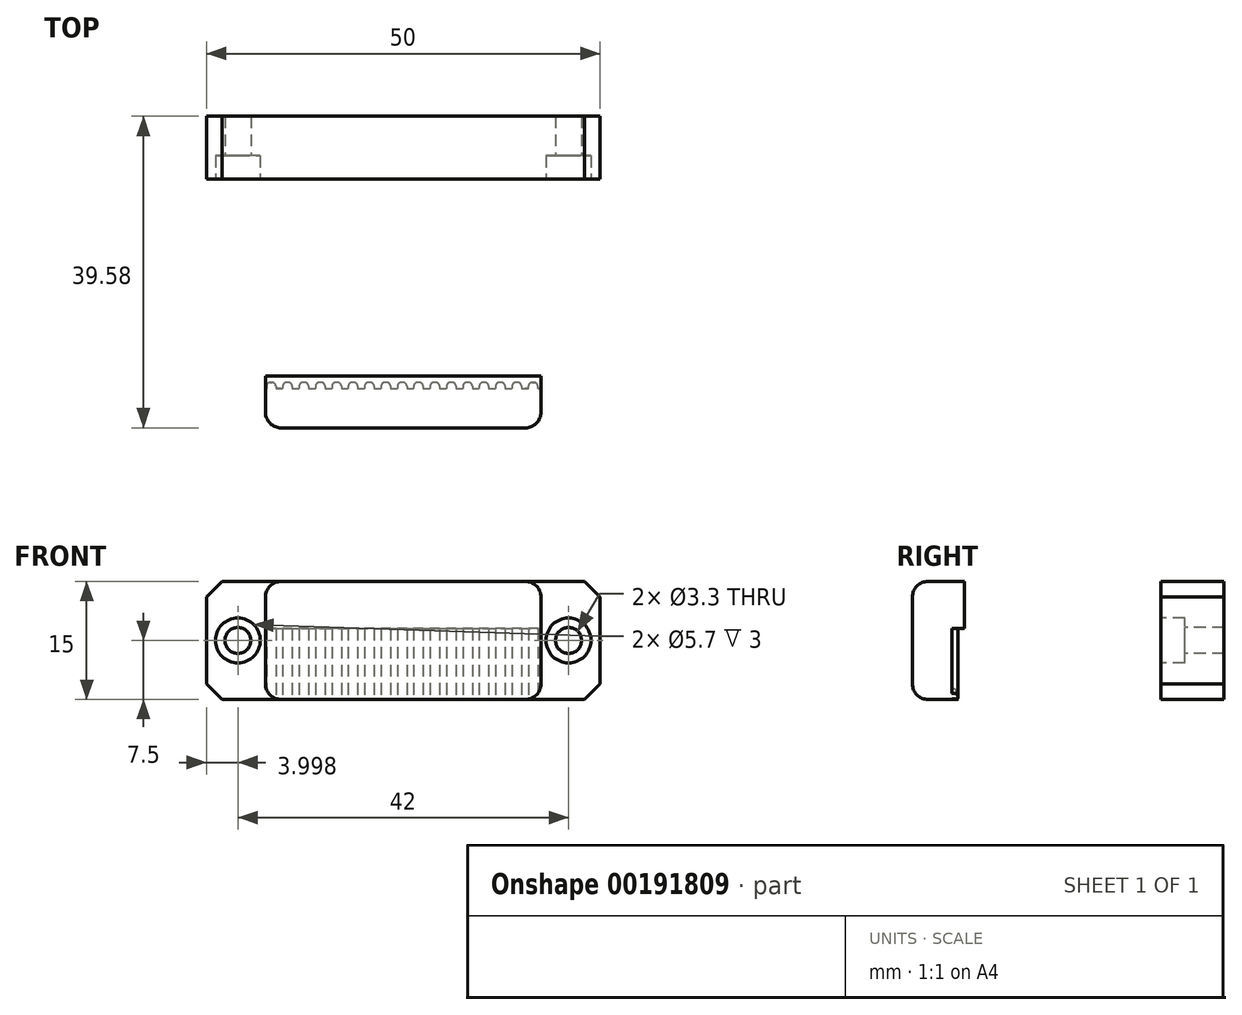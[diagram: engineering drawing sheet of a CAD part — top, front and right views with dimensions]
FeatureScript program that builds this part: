
annotation { "Feature Type Name" : "Feature", "Feature Type Description" : "" }
export const myFeature = defineFeature(function(context is Context, id is Id, definition is map)
    precondition{}
    {
        {
            var Q0;
            Q0=qCreatedBy(makeId("Top.planeOp"),FACE);
            var sketch = newSketch(context, id + "F0", { "sketchPlane" : qUnion([Q0])});
            skLineSegment(sketch, "E0.bottom", {"start": v(-21.77, 12.22) * mm, "end": v(28.23, 12.22) * mm});
            skLineSegment(sketch, "E0.top", {"start": v(-21.77, 4.22) * mm, "end": v(28.23, 4.22) * mm});
            skLineSegment(sketch, "E0.left", {"start": v(-21.77, 12.22) * mm, "end": v(-21.77, 4.22) * mm});
            skLineSegment(sketch, "E0.right", {"start": v(28.23, 12.22) * mm, "end": v(28.23, 4.22) * mm});
            skLineSegment(sketch, "E1.bottom", {"start": v(-14.27, 4.22) * mm, "end": v(20.73, 4.22) * mm});
            skLineSegment(sketch, "E1.top", {"start": v(-14.27, -20.78) * mm, "end": v(20.73, -20.78) * mm});
            skLineSegment(sketch, "E1.left", {"start": v(-14.27, 4.22) * mm, "end": v(-14.27, -20.78) * mm});
            skLineSegment(sketch, "E1.right", {"start": v(20.73, 4.22) * mm, "end": v(20.73, -20.78) * mm});
            skLineSegment(sketch, "E2.top", {"start": v(-14.27, -22.36) * mm, "end": v(20.73, -22.36) * mm});
            skLineSegment(sketch, "E2.left", {"start": v(-14.27, -20.78) * mm, "end": v(-14.27, -22.36) * mm});
            skLineSegment(sketch, "E2.right", {"start": v(20.73, -20.78) * mm, "end": v(20.73, -22.36) * mm});
            skLineSegment(sketch, "E3.top", {"start": v(-14.27, -27.36) * mm, "end": v(20.73, -27.36) * mm});
            skLineSegment(sketch, "E3.left", {"start": v(-14.27, -22.36) * mm, "end": v(-14.27, -27.36) * mm});
            skLineSegment(sketch, "E3.right", {"start": v(20.73, -22.36) * mm, "end": v(20.73, -27.36) * mm});
            skSolve(sketch);
        }
        {
            var Q0;
            Q0=makeQuery(id+"F0.imprint","IMPRINT",FACE,{"disambiguationData":[TD([[makeQuery(id+"F0.imprint","IMPRINT",EDGE,{"derivedFrom":sQuery(id+"F0.wireOp",EDGE,"E0.bottom")}),-1.0]])]});
            var Q1;
            Q1=makeQuery(id+"F0.imprint","IMPRINT",FACE,{"disambiguationData":[TD([[makeQuery(id+"F0.imprint","IMPRINT",EDGE,{"derivedFrom":sQuery(id+"F0.wireOp",EDGE,"E1.bottom")}),-1.0]])]});
            var Q2;
            Q2=makeQuery(id+"F0.imprint","IMPRINT",FACE,{"disambiguationData":[TD([[makeQuery(id+"F0.imprint","IMPRINT",EDGE,{"derivedFrom":sQuery(id+"F0.wireOp",EDGE,"E1.top")}),-1.0]])]});
            var Q3;
            Q3=makeQuery(id+"F0.imprint","IMPRINT",FACE,{"disambiguationData":[TD([[makeQuery(id+"F0.imprint","IMPRINT",EDGE,{"derivedFrom":sQuery(id+"F0.wireOp",EDGE,"E2.top")}),-1.0]])]});
            extrude(context, id + "F1", {"entities" : qUnion([Q0, Q1, Q2, Q3]), "depth" : 15 * mm});
        }
        {
            var Q0;
            Q0=makeQuery(id+"F0.imprint","IMPRINT",FACE,{"disambiguationData":[TD([[makeQuery(id+"F0.imprint","IMPRINT",EDGE,{"derivedFrom":sQuery(id+"F0.wireOp",EDGE,"E1.top")}),-1.0]])]});
            var sketch = newSketch(context, id + "F2", { "sketchPlane" : qUnion([Q0])});
            skLineSegment(sketch, "E4", {"start": v(19.88, -21.6) * mm, "end": v(-14.27, -21.6) * mm, "construction": true});
            skLineSegment(sketch, "E5.bottom", {"start": v(20.32, -21.6) * mm, "end": v(19.58, -21.6) * mm});
            skLineSegment(sketch, "E5.top", {"start": v(20.33, -22.36) * mm, "end": v(19.13, -22.36) * mm});
            skLineSegment(sketch, "E5.left", {"start": v(20.33, -22.06) * mm, "end": v(20.33, -22.36) * mm});
            skLineSegment(sketch, "E5.right", {"start": v(19.13, -22.06) * mm, "end": v(19.13, -22.36) * mm});
            skLineSegment(sketch, "E6.bottom", {"start": v(17.8, -21.6) * mm, "end": v(17.5, -21.6) * mm});
            skLineSegment(sketch, "E6.top", {"start": v(18.25, -22.36) * mm, "end": v(17.05, -22.36) * mm});
            skLineSegment(sketch, "E6.left", {"start": v(18.25, -22.06) * mm, "end": v(18.25, -22.36) * mm});
            skLineSegment(sketch, "E6.right", {"start": v(17.05, -22.06) * mm, "end": v(17.05, -22.36) * mm});
            skLineSegment(sketch, "E7.bottom", {"start": v(15.72, -21.6) * mm, "end": v(15.42, -21.6) * mm});
            skLineSegment(sketch, "E7.top", {"start": v(16.17, -22.36) * mm, "end": v(14.97, -22.36) * mm});
            skLineSegment(sketch, "E7.left", {"start": v(16.17, -22.06) * mm, "end": v(16.17, -22.36) * mm});
            skLineSegment(sketch, "E7.right", {"start": v(14.97, -22.06) * mm, "end": v(14.97, -22.36) * mm});
            skLineSegment(sketch, "E8.bottom", {"start": v(13.64, -21.6) * mm, "end": v(13.34, -21.6) * mm});
            skLineSegment(sketch, "E8.top", {"start": v(14.09, -22.36) * mm, "end": v(12.89, -22.36) * mm});
            skLineSegment(sketch, "E8.left", {"start": v(14.09, -22.06) * mm, "end": v(14.09, -22.36) * mm});
            skLineSegment(sketch, "E8.right", {"start": v(12.89, -22.06) * mm, "end": v(12.89, -22.36) * mm});
            skLineSegment(sketch, "E9.bottom", {"start": v(11.56, -21.6) * mm, "end": v(11.26, -21.6) * mm});
            skLineSegment(sketch, "E9.top", {"start": v(12, -22.36) * mm, "end": v(10.8, -22.36) * mm});
            skLineSegment(sketch, "E9.left", {"start": v(12, -22.06) * mm, "end": v(12, -22.36) * mm});
            skLineSegment(sketch, "E9.right", {"start": v(10.8, -22.06) * mm, "end": v(10.8, -22.36) * mm});
            skLineSegment(sketch, "E10.bottom", {"start": v(9.48, -21.6) * mm, "end": v(9.18, -21.6) * mm});
            skLineSegment(sketch, "E10.top", {"start": v(9.93, -22.36) * mm, "end": v(8.73, -22.36) * mm});
            skLineSegment(sketch, "E10.left", {"start": v(9.93, -22.06) * mm, "end": v(9.93, -22.36) * mm});
            skLineSegment(sketch, "E10.right", {"start": v(8.73, -22.06) * mm, "end": v(8.73, -22.36) * mm});
            skLineSegment(sketch, "E11.bottom", {"start": v(7.4, -21.6) * mm, "end": v(7.1, -21.6) * mm});
            skLineSegment(sketch, "E11.top", {"start": v(7.85, -22.36) * mm, "end": v(6.65, -22.36) * mm});
            skLineSegment(sketch, "E11.left", {"start": v(7.85, -22.06) * mm, "end": v(7.85, -22.36) * mm});
            skLineSegment(sketch, "E11.right", {"start": v(6.65, -22.06) * mm, "end": v(6.65, -22.36) * mm});
            skLineSegment(sketch, "E12.bottom", {"start": v(5.32, -21.6) * mm, "end": v(5.02, -21.6) * mm});
            skLineSegment(sketch, "E12.top", {"start": v(5.77, -22.36) * mm, "end": v(4.57, -22.36) * mm});
            skLineSegment(sketch, "E12.left", {"start": v(5.77, -22.06) * mm, "end": v(5.77, -22.36) * mm});
            skLineSegment(sketch, "E12.right", {"start": v(4.57, -22.06) * mm, "end": v(4.57, -22.36) * mm});
            skLineSegment(sketch, "E13.bottom", {"start": v(3.24, -21.6) * mm, "end": v(2.94, -21.6) * mm});
            skLineSegment(sketch, "E13.top", {"start": v(3.69, -22.36) * mm, "end": v(2.49, -22.36) * mm});
            skLineSegment(sketch, "E13.left", {"start": v(3.69, -22.06) * mm, "end": v(3.69, -22.36) * mm});
            skLineSegment(sketch, "E13.right", {"start": v(2.49, -22.06) * mm, "end": v(2.49, -22.36) * mm});
            skLineSegment(sketch, "E14.bottom", {"start": v(1.16, -21.6) * mm, "end": v(0.86, -21.6) * mm});
            skLineSegment(sketch, "E14.top", {"start": v(1.6, -22.36) * mm, "end": v(0.4, -22.36) * mm});
            skLineSegment(sketch, "E14.left", {"start": v(1.6, -22.06) * mm, "end": v(1.6, -22.36) * mm});
            skLineSegment(sketch, "E14.right", {"start": v(0.4, -22.06) * mm, "end": v(0.4, -22.36) * mm});
            skLineSegment(sketch, "E15.bottom", {"start": v(-0.92, -21.6) * mm, "end": v(-1.22, -21.6) * mm});
            skLineSegment(sketch, "E15.top", {"start": v(-0.47, -22.36) * mm, "end": v(-1.67, -22.36) * mm});
            skLineSegment(sketch, "E15.left", {"start": v(-0.47, -22.06) * mm, "end": v(-0.47, -22.36) * mm});
            skLineSegment(sketch, "E15.right", {"start": v(-1.67, -22.06) * mm, "end": v(-1.67, -22.36) * mm});
            skLineSegment(sketch, "E16.bottom", {"start": v(-3, -21.6) * mm, "end": v(-3.3, -21.6) * mm});
            skLineSegment(sketch, "E16.top", {"start": v(-2.55, -22.36) * mm, "end": v(-3.75, -22.36) * mm});
            skLineSegment(sketch, "E16.left", {"start": v(-2.55, -22.06) * mm, "end": v(-2.55, -22.36) * mm});
            skLineSegment(sketch, "E16.right", {"start": v(-3.75, -22.06) * mm, "end": v(-3.75, -22.36) * mm});
            skLineSegment(sketch, "E17.bottom", {"start": v(-5.08, -21.6) * mm, "end": v(-5.38, -21.6) * mm});
            skLineSegment(sketch, "E17.top", {"start": v(-4.63, -22.36) * mm, "end": v(-5.83, -22.36) * mm});
            skLineSegment(sketch, "E17.left", {"start": v(-4.63, -22.06) * mm, "end": v(-4.63, -22.36) * mm});
            skLineSegment(sketch, "E17.right", {"start": v(-5.83, -22.06) * mm, "end": v(-5.83, -22.36) * mm});
            skLineSegment(sketch, "E18.bottom", {"start": v(-7.16, -21.6) * mm, "end": v(-7.46, -21.6) * mm});
            skLineSegment(sketch, "E18.top", {"start": v(-6.71, -22.36) * mm, "end": v(-7.91, -22.36) * mm});
            skLineSegment(sketch, "E18.left", {"start": v(-6.71, -22.06) * mm, "end": v(-6.71, -22.36) * mm});
            skLineSegment(sketch, "E18.right", {"start": v(-7.91, -22.06) * mm, "end": v(-7.91, -22.36) * mm});
            skLineSegment(sketch, "E19.bottom", {"start": v(-9.24, -21.6) * mm, "end": v(-9.54, -21.6) * mm});
            skLineSegment(sketch, "E19.top", {"start": v(-8.8, -22.36) * mm, "end": v(-10, -22.36) * mm});
            skLineSegment(sketch, "E19.left", {"start": v(-8.8, -22.06) * mm, "end": v(-8.8, -22.36) * mm});
            skLineSegment(sketch, "E19.right", {"start": v(-10, -22.06) * mm, "end": v(-10, -22.36) * mm});
            skLineSegment(sketch, "E20.bottom", {"start": v(-11.32, -21.6) * mm, "end": v(-11.62, -21.6) * mm});
            skLineSegment(sketch, "E20.top", {"start": v(-10.87, -22.36) * mm, "end": v(-12.07, -22.36) * mm});
            skLineSegment(sketch, "E20.left", {"start": v(-10.87, -22.06) * mm, "end": v(-10.87, -22.36) * mm});
            skLineSegment(sketch, "E20.right", {"start": v(-12.07, -22.06) * mm, "end": v(-12.07, -22.36) * mm});
            skLineSegment(sketch, "E21.bottom", {"start": v(-13.4, -21.6) * mm, "end": v(-13.7, -21.6) * mm});
            skLineSegment(sketch, "E21.top", {"start": v(-12.95, -22.36) * mm, "end": v(-14.15, -22.36) * mm});
            skLineSegment(sketch, "E21.left", {"start": v(-12.95, -22.06) * mm, "end": v(-12.95, -22.36) * mm});
            skLineSegment(sketch, "E21.right", {"start": v(-14.15, -22.06) * mm, "end": v(-14.15, -22.36) * mm});
            skLineSegment(sketch, "E22.bottom", {"start": v(-12.41, -21.6) * mm, "end": v(-13.61, -21.6) * mm});
            skPoint(sketch, "E23.newPointB", {"position": v(20.73, -21.6) * mm});
            skArc(sketch, "E23.filletArc", {"start": v(20.33, -22.06) * mm, "mid": v(20.2, -21.74) * mm, "end": v(19.88, -21.6) * mm});
            skPoint(sketch, "E24.visualSharp", {"position": v(19.13, -21.6) * mm});
            skArc(sketch, "E24.filletArc", {"start": v(19.58, -21.6) * mm, "mid": v(19.26, -21.74) * mm, "end": v(19.13, -22.06) * mm});
            skPoint(sketch, "E25.visualSharp", {"position": v(18.25, -21.6) * mm});
            skArc(sketch, "E25.filletArc", {"start": v(18.25, -22.06) * mm, "mid": v(18.12, -21.74) * mm, "end": v(17.8, -21.6) * mm});
            skPoint(sketch, "E26.visualSharp", {"position": v(17.05, -21.6) * mm});
            skArc(sketch, "E26.filletArc", {"start": v(17.5, -21.6) * mm, "mid": v(17.18, -21.74) * mm, "end": v(17.05, -22.06) * mm});
            skPoint(sketch, "E27.visualSharp", {"position": v(16.17, -21.6) * mm});
            skArc(sketch, "E27.filletArc", {"start": v(16.17, -22.06) * mm, "mid": v(16.04, -21.74) * mm, "end": v(15.72, -21.6) * mm});
            skPoint(sketch, "E28.visualSharp", {"position": v(14.97, -21.6) * mm});
            skArc(sketch, "E28.filletArc", {"start": v(15.42, -21.6) * mm, "mid": v(15.1, -21.74) * mm, "end": v(14.97, -22.06) * mm});
            skPoint(sketch, "E29.visualSharp", {"position": v(14.09, -21.6) * mm});
            skArc(sketch, "E29.filletArc", {"start": v(14.09, -22.06) * mm, "mid": v(13.96, -21.74) * mm, "end": v(13.64, -21.6) * mm});
            skPoint(sketch, "E30.visualSharp", {"position": v(12.89, -21.6) * mm});
            skArc(sketch, "E30.filletArc", {"start": v(13.34, -21.6) * mm, "mid": v(13.02, -21.74) * mm, "end": v(12.89, -22.06) * mm});
            skPoint(sketch, "E31.visualSharp", {"position": v(12, -21.6) * mm});
            skArc(sketch, "E31.filletArc", {"start": v(12, -22.06) * mm, "mid": v(11.88, -21.74) * mm, "end": v(11.56, -21.6) * mm});
            skPoint(sketch, "E32.visualSharp", {"position": v(10.8, -21.6) * mm});
            skArc(sketch, "E32.filletArc", {"start": v(11.26, -21.6) * mm, "mid": v(10.94, -21.74) * mm, "end": v(10.8, -22.06) * mm});
            skPoint(sketch, "E33.visualSharp", {"position": v(9.93, -21.6) * mm});
            skArc(sketch, "E33.filletArc", {"start": v(9.93, -22.06) * mm, "mid": v(9.8, -21.74) * mm, "end": v(9.48, -21.6) * mm});
            skPoint(sketch, "E34.visualSharp", {"position": v(8.73, -21.6) * mm});
            skArc(sketch, "E34.filletArc", {"start": v(9.18, -21.6) * mm, "mid": v(8.86, -21.74) * mm, "end": v(8.73, -22.06) * mm});
            skPoint(sketch, "E35.visualSharp", {"position": v(7.85, -21.6) * mm});
            skArc(sketch, "E35.filletArc", {"start": v(7.85, -22.06) * mm, "mid": v(7.72, -21.74) * mm, "end": v(7.4, -21.6) * mm});
            skPoint(sketch, "E36.visualSharp", {"position": v(6.65, -21.6) * mm});
            skArc(sketch, "E36.filletArc", {"start": v(7.1, -21.6) * mm, "mid": v(6.78, -21.74) * mm, "end": v(6.65, -22.06) * mm});
            skPoint(sketch, "E37.visualSharp", {"position": v(5.77, -21.6) * mm});
            skArc(sketch, "E37.filletArc", {"start": v(5.77, -22.06) * mm, "mid": v(5.64, -21.74) * mm, "end": v(5.32, -21.6) * mm});
            skPoint(sketch, "E38.visualSharp", {"position": v(4.57, -21.6) * mm});
            skArc(sketch, "E38.filletArc", {"start": v(5.02, -21.6) * mm, "mid": v(4.7, -21.74) * mm, "end": v(4.57, -22.06) * mm});
            skPoint(sketch, "E39.visualSharp", {"position": v(3.69, -21.6) * mm});
            skArc(sketch, "E39.filletArc", {"start": v(3.69, -22.06) * mm, "mid": v(3.56, -21.74) * mm, "end": v(3.24, -21.6) * mm});
            skPoint(sketch, "E40.visualSharp", {"position": v(1.6, -21.6) * mm});
            skArc(sketch, "E40.filletArc", {"start": v(1.6, -22.06) * mm, "mid": v(1.48, -21.74) * mm, "end": v(1.16, -21.6) * mm});
            skPoint(sketch, "E41.visualSharp", {"position": v(2.49, -21.6) * mm});
            skArc(sketch, "E41.filletArc", {"start": v(2.94, -21.6) * mm, "mid": v(2.62, -21.74) * mm, "end": v(2.49, -22.06) * mm});
            skPoint(sketch, "E42.visualSharp", {"position": v(0.4, -21.6) * mm});
            skArc(sketch, "E42.filletArc", {"start": v(0.86, -21.6) * mm, "mid": v(0.54, -21.74) * mm, "end": v(0.4, -22.06) * mm});
            skPoint(sketch, "E43.visualSharp", {"position": v(-0.47, -21.6) * mm});
            skArc(sketch, "E43.filletArc", {"start": v(-0.47, -22.06) * mm, "mid": v(-0.6, -21.74) * mm, "end": v(-0.92, -21.6) * mm});
            skPoint(sketch, "E44.visualSharp", {"position": v(-1.67, -21.6) * mm});
            skArc(sketch, "E44.filletArc", {"start": v(-1.22, -21.6) * mm, "mid": v(-1.54, -21.74) * mm, "end": v(-1.67, -22.06) * mm});
            skPoint(sketch, "E45.visualSharp", {"position": v(-2.55, -21.6) * mm});
            skArc(sketch, "E45.filletArc", {"start": v(-2.55, -22.06) * mm, "mid": v(-2.68, -21.74) * mm, "end": v(-3, -21.6) * mm});
            skPoint(sketch, "E46.visualSharp", {"position": v(-3.75, -21.6) * mm});
            skArc(sketch, "E46.filletArc", {"start": v(-3.3, -21.6) * mm, "mid": v(-3.62, -21.74) * mm, "end": v(-3.75, -22.06) * mm});
            skPoint(sketch, "E47.visualSharp", {"position": v(-4.63, -21.6) * mm});
            skArc(sketch, "E47.filletArc", {"start": v(-4.63, -22.06) * mm, "mid": v(-4.76, -21.74) * mm, "end": v(-5.08, -21.6) * mm});
            skPoint(sketch, "E48.visualSharp", {"position": v(-5.83, -21.6) * mm});
            skArc(sketch, "E48.filletArc", {"start": v(-5.38, -21.6) * mm, "mid": v(-5.7, -21.74) * mm, "end": v(-5.83, -22.06) * mm});
            skPoint(sketch, "E49.visualSharp", {"position": v(-6.71, -21.6) * mm});
            skArc(sketch, "E49.filletArc", {"start": v(-6.71, -22.06) * mm, "mid": v(-6.84, -21.74) * mm, "end": v(-7.16, -21.6) * mm});
            skPoint(sketch, "E50.visualSharp", {"position": v(-7.91, -21.6) * mm});
            skArc(sketch, "E50.filletArc", {"start": v(-7.46, -21.6) * mm, "mid": v(-7.78, -21.74) * mm, "end": v(-7.91, -22.06) * mm});
            skPoint(sketch, "E51.visualSharp", {"position": v(-8.8, -21.6) * mm});
            skArc(sketch, "E51.filletArc", {"start": v(-8.8, -22.06) * mm, "mid": v(-8.92, -21.74) * mm, "end": v(-9.24, -21.6) * mm});
            skPoint(sketch, "E52.visualSharp", {"position": v(-10, -21.6) * mm});
            skArc(sketch, "E52.filletArc", {"start": v(-9.54, -21.6) * mm, "mid": v(-9.86, -21.74) * mm, "end": v(-10, -22.06) * mm});
            skPoint(sketch, "E53.visualSharp", {"position": v(-10.87, -21.6) * mm});
            skArc(sketch, "E53.filletArc", {"start": v(-10.87, -22.06) * mm, "mid": v(-11, -21.74) * mm, "end": v(-11.32, -21.6) * mm});
            skPoint(sketch, "E54.visualSharp", {"position": v(-12.07, -21.6) * mm});
            skArc(sketch, "E54.filletArc", {"start": v(-11.62, -21.6) * mm, "mid": v(-11.94, -21.74) * mm, "end": v(-12.07, -22.06) * mm});
            skPoint(sketch, "E55.visualSharp", {"position": v(-12.95, -21.6) * mm});
            skArc(sketch, "E55.filletArc", {"start": v(-12.95, -22.06) * mm, "mid": v(-13.08, -21.74) * mm, "end": v(-13.4, -21.6) * mm});
            skPoint(sketch, "E56.visualSharp", {"position": v(-14.15, -21.6) * mm});
            skArc(sketch, "E56.filletArc", {"start": v(-13.7, -21.6) * mm, "mid": v(-14.02, -21.74) * mm, "end": v(-14.15, -22.06) * mm});
            skSolve(sketch);
        }
        {
            var Q0;
            {var subQ10=sQuery(id+"F2.wireOp",EDGE,"E5.left");Q0=makeQuery(id+"F2.imprint","IMPRINT",FACE,{"disambiguationData":[TD([[makeQuery(id+"F2.imprint","IMPRINT",EDGE,{"derivedFrom":subQ10}),1.0]])]});}
            extrude(context, id + "F3", {"entities" : qUnion([Q0]), "operationType" : NewBodyOperationType.REMOVE, "depth" : 9 * mm});
        }
        {
            var Q0;
            {var subQ0=sQuery(id+"F0.wireOp",EDGE,"E3.left");var subQ1=sQuery(id+"F0.wireOp",EDGE,"E2.left");var subQ2=sQuery(id+"F0.wireOp",EDGE,"E1.left");Q0=makeQuery(id+"F3.boolean.opBoolean","SPLIT",EDGE,{"disambiguationData":[TD([makeQuery(id+"F3.opExtrude","SWEPT_FACE",FACE,{"disambiguationData":[OSD([sQuery(id+"F0.wireOp",EDGE,"E1.top")])]})])],"derivedFrom":makeQuery(id+"F1.opExtrude","CAP_EDGE",EDGE,{"disambiguationData":[OSD([subQ2,subQ1,subQ0])],"isStart":true})});}
            var Q1;
            Q1=makeQuery(id+"F1.opExtrude","CAP_EDGE",EDGE,{"disambiguationData":[OSD([sQuery(id+"F0.wireOp",EDGE,"E1.left"),sQuery(id+"F0.wireOp",EDGE,"E2.left"),sQuery(id+"F0.wireOp",EDGE,"E3.left")])],"isStart":false});
            var Q2;
            Q2=makeQuery(id+"F1.opExtrude","CAP_EDGE",EDGE,{"disambiguationData":[OSD([sQuery(id+"F0.wireOp",EDGE,"E1.right"),sQuery(id+"F0.wireOp",EDGE,"E2.right"),sQuery(id+"F0.wireOp",EDGE,"E3.right")])],"isStart":false});
            var Q3;
            {var subQ0=sQuery(id+"F0.wireOp",EDGE,"E3.right");var subQ1=sQuery(id+"F0.wireOp",EDGE,"E2.right");var subQ2=sQuery(id+"F0.wireOp",EDGE,"E1.right");Q3=makeQuery(id+"F3.boolean.opBoolean","SPLIT",EDGE,{"disambiguationData":[TD([makeQuery(id+"F3.opExtrude","SWEPT_FACE",FACE,{"disambiguationData":[OSD([sQuery(id+"F0.wireOp",EDGE,"E1.top")])]})])],"derivedFrom":makeQuery(id+"F1.opExtrude","CAP_EDGE",EDGE,{"disambiguationData":[OSD([subQ2,subQ1,subQ0])],"isStart":true})});}
            var Q4;
            Q4=makeQuery(id+"F1.opExtrude","CAP_EDGE",EDGE,{"disambiguationData":[OSD([sQuery(id+"F0.wireOp",EDGE,"E3.top")])],"isStart":true});
            var Q5;
            Q5=makeQuery(id+"F1.opExtrude","CAP_EDGE",EDGE,{"disambiguationData":[OSD([sQuery(id+"F0.wireOp",EDGE,"E3.top")])],"isStart":false});
            var Q6;
            Q6=makeQuery(id+"F1.opExtrude","SWEPT_EDGE",EDGE,{"disambiguationData":[OSD([sQuery(id+"F0.wireOp",EDGE,"E3.top"),sQuery(id+"F0.wireOp",EDGE,"E3.right")])]});
            var Q7;
            Q7=makeQuery(id+"F1.opExtrude","SWEPT_EDGE",EDGE,{"disambiguationData":[OSD([sQuery(id+"F0.wireOp",EDGE,"E3.top"),sQuery(id+"F0.wireOp",EDGE,"E3.left")])]});
            var Q8;
            {var subQ0=sQuery(id+"F0.wireOp",EDGE,"E3.right");var subQ1=sQuery(id+"F0.wireOp",EDGE,"E3.top");var subQ2=sQuery(id+"F0.wireOp",EDGE,"E2.right");var subQ3=sQuery(id+"F0.wireOp",EDGE,"E1.right");Q8=makeQuery(id+"F3.boolean.opBoolean","SPLIT",EDGE,{"disambiguationData":[TD([makeQuery(id+"F1.opExtrude","SWEPT_FACE",FACE,{"disambiguationData":[OSD([subQ1])]})])],"derivedFrom":makeQuery(id+"F1.opExtrude","CAP_EDGE",EDGE,{"disambiguationData":[OSD([subQ3,subQ2,subQ0])],"isStart":true})});}
            var Q9;
            {var subQ0=sQuery(id+"F0.wireOp",EDGE,"E3.left");var subQ1=sQuery(id+"F0.wireOp",EDGE,"E3.top");var subQ2=sQuery(id+"F0.wireOp",EDGE,"E2.left");var subQ3=sQuery(id+"F0.wireOp",EDGE,"E1.left");Q9=makeQuery(id+"F3.boolean.opBoolean","SPLIT",EDGE,{"disambiguationData":[TD([makeQuery(id+"F1.opExtrude","SWEPT_FACE",FACE,{"disambiguationData":[OSD([subQ1])]})])],"derivedFrom":makeQuery(id+"F1.opExtrude","CAP_EDGE",EDGE,{"disambiguationData":[OSD([subQ3,subQ2,subQ0])],"isStart":true})});}
            fillet(context, id + "F4", {"entities" : qUnion([Q0, Q1, Q2, Q3, Q4, Q5, Q6, Q7, Q8, Q9]), "radius" : 2 * mm, "tangentPropagation" : true, "allowEdgeOverflow" : false});
        }
        {
            var Q0;
            {var subQ0=sQuery(id+"F0.wireOp",EDGE,"E0.top");Q0=makeQuery(id+"F1.opExtrude","SWEPT_FACE",FACE,{"disambiguationData":[OSD([subQ0]),TDD([makeQuery(id+"F0.imprint","IMPRINT",EDGE,{"disambiguationData":[TD([[makeQuery(id+"F0.imprint","INTERSECT",VERTEX,{"derivedFrom":[subQ0,sQuery(id+"F0.wireOp",EDGE,"E0.right")]}),1.0]])],"derivedFrom":subQ0})])]});}
            var sketch = newSketch(context, id + "F5", { "sketchPlane" : qUnion([Q0])});
            skCircle(sketch, "E57", {"center": v(24.23, 7.5) * mm, "radius": 1.65 * mm});
            skCircle(sketch, "E58", {"center": v(24.23, 7.5) * mm, "radius": 2.85 * mm});
            skSolve(sketch);
        }
        {
            var Q0;
            Q0=makeQuery(id+"F1.opExtrude","CAP_EDGE",EDGE,{"disambiguationData":[OSD([sQuery(id+"F0.wireOp",EDGE,"E0.left")])],"isStart":true});
            var Q1;
            Q1=makeQuery(id+"F1.opExtrude","CAP_EDGE",EDGE,{"disambiguationData":[OSD([sQuery(id+"F0.wireOp",EDGE,"E0.left")])],"isStart":false});
            var Q2;
            Q2=makeQuery(id+"F1.opExtrude","CAP_EDGE",EDGE,{"disambiguationData":[OSD([sQuery(id+"F0.wireOp",EDGE,"E0.right")])],"isStart":true});
            var Q3;
            Q3=makeQuery(id+"F1.opExtrude","CAP_EDGE",EDGE,{"disambiguationData":[OSD([sQuery(id+"F0.wireOp",EDGE,"E0.right")])],"isStart":false});
            chamfer(context, id + "F6", {"entities" : qUnion([Q0, Q1, Q2, Q3]), "width" : 2 * mm, "tangentPropagation" : true});
        }
        {
            var Q0;
            {var subQ0=sQuery(id+"F0.wireOp",EDGE,"E0.top");Q0=makeQuery(id+"F1.opExtrude","SWEPT_FACE",FACE,{"disambiguationData":[OSD([subQ0]),TDD([makeQuery(id+"F0.imprint","IMPRINT",EDGE,{"disambiguationData":[TD([[makeQuery(id+"F0.imprint","INTERSECT",VERTEX,{"derivedFrom":[subQ0,sQuery(id+"F0.wireOp",EDGE,"E0.left")]}),-1.0]])],"derivedFrom":subQ0})])]});}
            var sketch = newSketch(context, id + "F7", { "sketchPlane" : qUnion([Q0])});
            skCircle(sketch, "E59", {"center": v(-17.77, 7.5) * mm, "radius": 2.85 * mm});
            skCircle(sketch, "E60", {"center": v(-17.77, 7.5) * mm, "radius": 1.65 * mm});
            skSolve(sketch);
        }
        {
            var Q0;
            Q0=makeQuery(id+"F5.imprint","IMPRINT",FACE,{"disambiguationData":[TD([[makeQuery(id+"F5.imprint","IMPRINT",EDGE,{"derivedFrom":sQuery(id+"F5.wireOp",EDGE,"E57")}),1.0]])]});
            var Q1;
            Q1=makeQuery(id+"F7.imprint","IMPRINT",FACE,{"disambiguationData":[TD([[makeQuery(id+"F7.imprint","IMPRINT",EDGE,{"derivedFrom":sQuery(id+"F7.wireOp",EDGE,"E60")}),1.0]])]});
            extrude(context, id + "F8", {"entities" : qUnion([Q0, Q1]), "operationType" : NewBodyOperationType.REMOVE, "endBound" : BoundingType.UP_TO_NEXT, "oppositeDirection" : true, "depth" : 25 * mm});
        }
        {
            var Q0;
            Q0=makeQuery(id+"F5.imprint","IMPRINT",FACE,{"disambiguationData":[TD([[makeQuery(id+"F5.imprint","IMPRINT",EDGE,{"derivedFrom":sQuery(id+"F5.wireOp",EDGE,"E57")}),-1.0]])]});
            var Q1;
            Q1=makeQuery(id+"F7.imprint","IMPRINT",FACE,{"disambiguationData":[TD([[makeQuery(id+"F7.imprint","IMPRINT",EDGE,{"derivedFrom":sQuery(id+"F7.wireOp",EDGE,"E59")}),1.0]])]});
            extrude(context, id + "F9", {"entities" : qUnion([Q0, Q1]), "operationType" : NewBodyOperationType.REMOVE, "oppositeDirection" : true, "depth" : 3 * mm});
        }
    });
